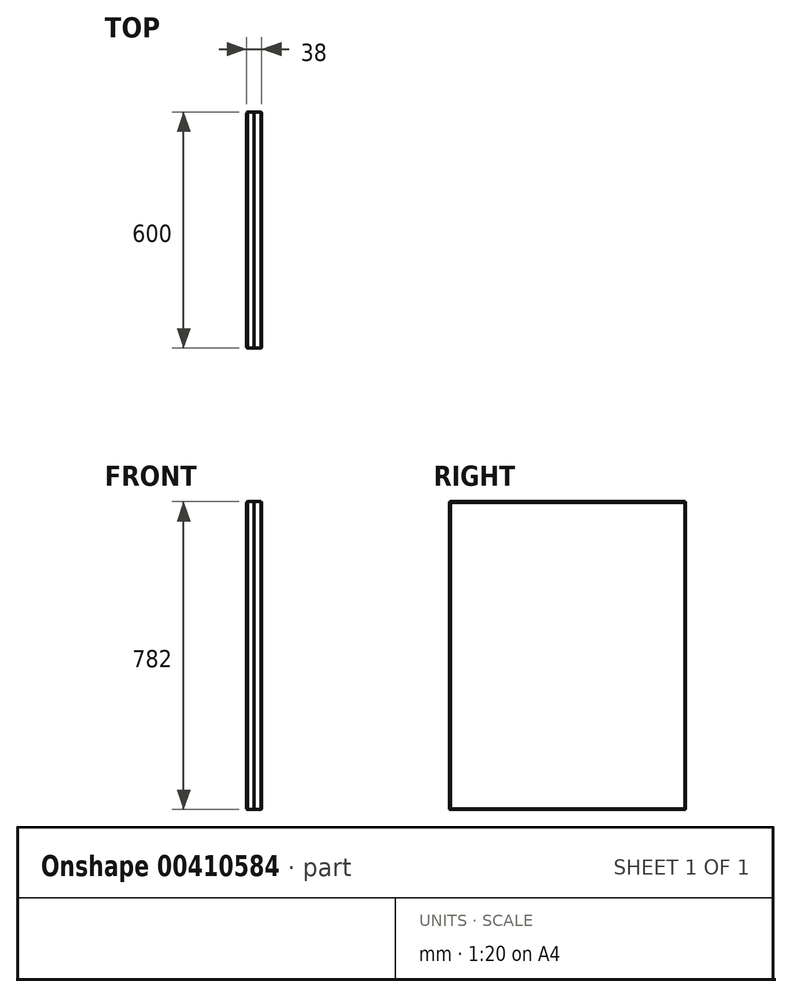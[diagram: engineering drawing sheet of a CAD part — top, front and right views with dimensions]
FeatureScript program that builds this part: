
annotation { "Feature Type Name" : "Feature", "Feature Type Description" : "" }
export const myFeature = defineFeature(function(context is Context, id is Id, definition is map)
    precondition{}
    {
        {
            var Q0;
            Q0=qCreatedBy(makeId("Right.planeOp"),FACE);
            var sketch = newSketch(context, id + "F0", { "sketchPlane" : qUnion([Q0])});
            skLineSegment(sketch, "E0.bottom", {"start": v(-298, 391) * mm, "end": v(298, 391) * mm});
            skLineSegment(sketch, "E0.top", {"start": v(-298, -391) * mm, "end": v(298, -391) * mm});
            skLineSegment(sketch, "E0.left", {"start": v(-300, 389) * mm, "end": v(-300, -389) * mm});
            skLineSegment(sketch, "E0.right", {"start": v(300, 389) * mm, "end": v(300, -389) * mm});
            skPoint(sketch, "E0.middle", {"position": v(0, 0) * mm});
            skPoint(sketch, "E1.visualSharp", {"position": v(-300, 391) * mm});
            skArc(sketch, "E1.filletArc", {"start": v(-298, 391) * mm, "mid": v(-299.41, 390.41) * mm, "end": v(-300, 389) * mm});
            skPoint(sketch, "E2.visualSharp", {"position": v(300, 391) * mm});
            skArc(sketch, "E2.filletArc", {"start": v(300, 389) * mm, "mid": v(299.41, 390.41) * mm, "end": v(298, 391) * mm});
            skPoint(sketch, "E3.visualSharp", {"position": v(-300, -391) * mm});
            skArc(sketch, "E3.filletArc", {"start": v(-300, -389) * mm, "mid": v(-299.41, -390.41) * mm, "end": v(-298, -391) * mm});
            skPoint(sketch, "E4.visualSharp", {"position": v(300, -391) * mm});
            skArc(sketch, "E4.filletArc", {"start": v(298, -391) * mm, "mid": v(299.41, -390.41) * mm, "end": v(300, -389) * mm});
            skSolve(sketch);
        }
        {
            var Q0;
            Q0=makeQuery(id+"F0.imprint","IMPRINT",FACE,{"disambiguationData":[TD([[makeQuery(id+"F0.imprint","IMPRINT",EDGE,{"derivedFrom":sQuery(id+"F0.wireOp",EDGE,"E0.bottom")}),-1.0]])]});
            extrude(context, id + "F1", {"entities" : qUnion([Q0]), "depth" : 19 * mm});
        }
        {
            var Q0;
            Q0=makeQuery(id+"F1.opExtrude","CAP_EDGE",EDGE,{"disambiguationData":[OSD([sQuery(id+"F0.wireOp",EDGE,"E0.bottom")])],"isStart":true});
            var Q1;
            Q1=makeQuery(id+"F1.opExtrude","CAP_EDGE",EDGE,{"disambiguationData":[OSD([sQuery(id+"F0.wireOp",EDGE,"E0.left")])],"isStart":true});
            var Q2;
            Q2=makeQuery(id+"F1.opExtrude","CAP_EDGE",EDGE,{"disambiguationData":[OSD([sQuery(id+"F0.wireOp",EDGE,"E0.top")])],"isStart":true});
            var Q3;
            Q3=makeQuery(id+"F1.opExtrude","CAP_EDGE",EDGE,{"disambiguationData":[OSD([sQuery(id+"F0.wireOp",EDGE,"E0.right")])],"isStart":true});
            chamfer(context, id + "F2", {"entities" : qUnion([Q0, Q1, Q2, Q3]), "chamferType" : ChamferType.TWO_OFFSETS, "width1" : 2 * mm, "oppositeDirection" : false, "width2" : 2 * mm});
        }
        {
            var Q0;
            Q0=makeQuery(id+"F1.opExtrude","SWEPT_BODY",BODY,{"disambiguationData":[OSD([sQuery(id+"F0.wireOp",EDGE,"E0.bottom"),sQuery(id+"F0.wireOp",EDGE,"E0.top"),sQuery(id+"F0.wireOp",EDGE,"E0.left"),sQuery(id+"F0.wireOp",EDGE,"E0.right"),sQuery(id+"F0.wireOp",EDGE,"E1.filletArc"),sQuery(id+"F0.wireOp",EDGE,"E2.filletArc"),sQuery(id+"F0.wireOp",EDGE,"E3.filletArc"),sQuery(id+"F0.wireOp",EDGE,"E4.filletArc")])]});
            var Q1;
            Q1=makeQuery(id+"F1.opExtrude","CAP_FACE",FACE,{"disambiguationData":[OSD([sQuery(id+"F0.wireOp",EDGE,"E0.bottom"),sQuery(id+"F0.wireOp",EDGE,"E0.top"),sQuery(id+"F0.wireOp",EDGE,"E0.left"),sQuery(id+"F0.wireOp",EDGE,"E0.right"),sQuery(id+"F0.wireOp",EDGE,"E1.filletArc"),sQuery(id+"F0.wireOp",EDGE,"E2.filletArc"),sQuery(id+"F0.wireOp",EDGE,"E3.filletArc"),sQuery(id+"F0.wireOp",EDGE,"E4.filletArc")])],"isStart":false});
            mirror(context, id + "F3", {"entities" : qUnion([Q0]), "mirrorPlane" : qUnion([Q1])});
        }
    });
